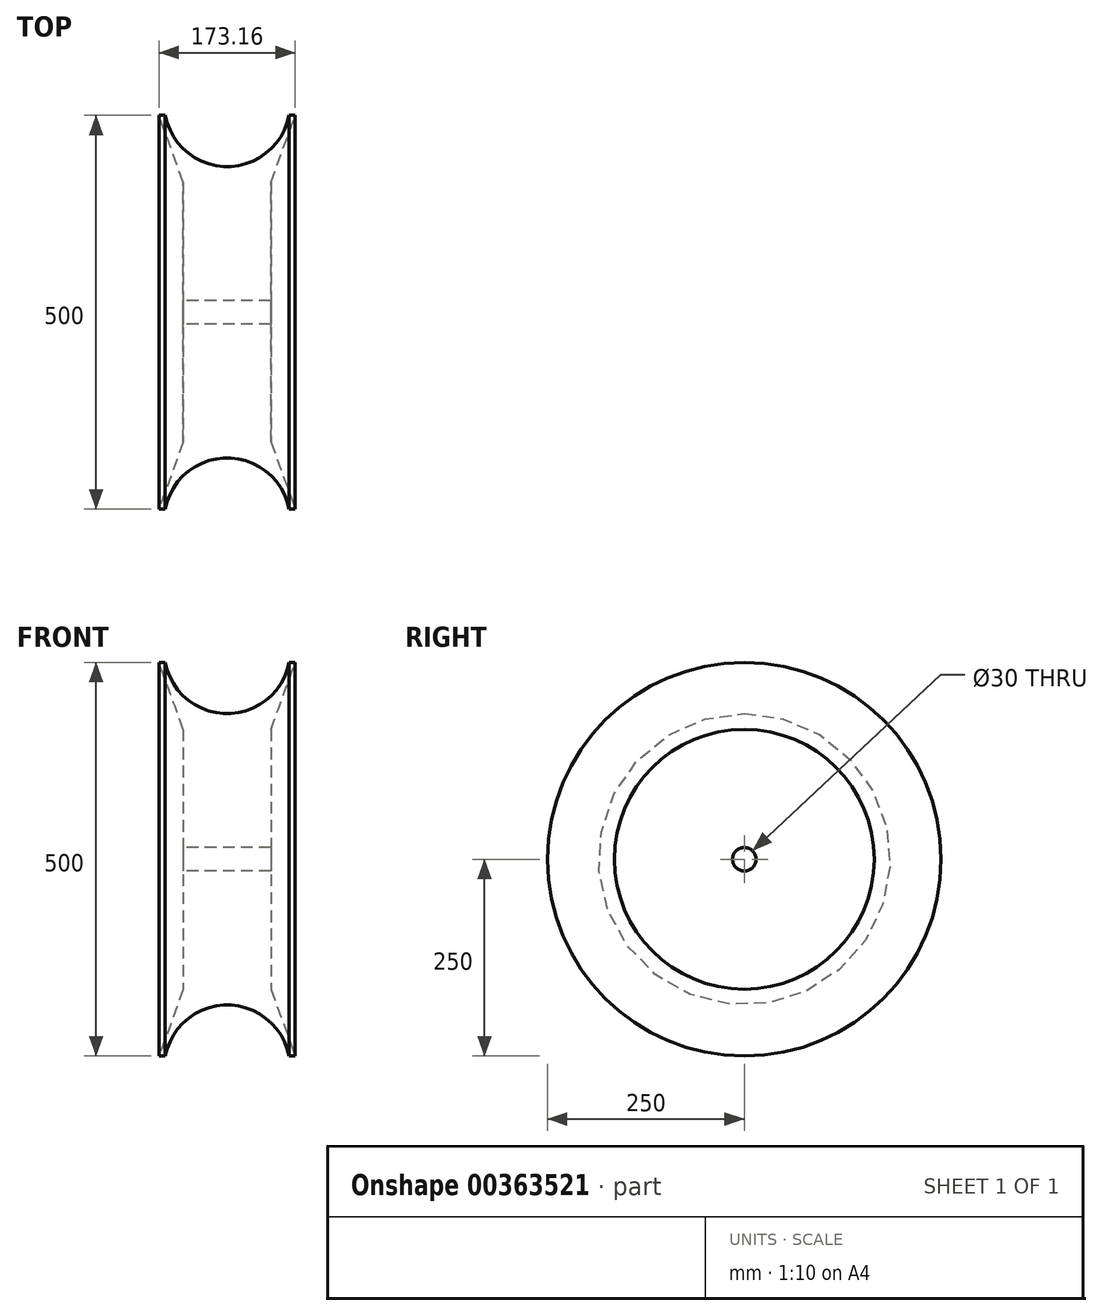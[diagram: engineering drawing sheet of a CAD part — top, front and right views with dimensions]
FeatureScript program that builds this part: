
annotation { "Feature Type Name" : "Feature", "Feature Type Description" : "" }
export const myFeature = defineFeature(function(context is Context, id is Id, definition is map)
    precondition{}
    {
        {
            var Q0;
            Q0=qCreatedBy(makeId("Front.planeOp"),FACE);
            var sketch = newSketch(context, id + "F0", { "sketchPlane" : qUnion([Q0])});
            skLineSegment(sketch, "E0", {"start": v(55.64, 15) * mm, "end": v(55.64, 165) * mm});
            skLineSegment(sketch, "E1", {"start": v(55.64, 165) * mm, "end": v(86.58, 250) * mm});
            skLineSegment(sketch, "E2", {"start": v(0, -26.36) * mm, "end": v(0, 300.42) * mm, "construction": true});
            skLineSegment(sketch, "E3", {"start": v(86.58, 250) * mm, "end": v(78.58, 250) * mm});
            skArc(sketch, "E4", {"start": v(0, 185) * mm, "mid": v(51, 203.36) * mm, "end": v(78.58, 250) * mm});
            skLineSegment(sketch, "E5", {"start": v(0, 185) * mm, "end": v(0, 0) * mm});
            skLineSegment(sketch, "E6", {"start": v(0, 15) * mm, "end": v(55.64, 15) * mm});
            skLineSegment(sketch, "E7", {"start": v(-86.07, 0) * mm, "end": v(75.22, 0) * mm, "construction": true});
            skSolve(sketch);
        }
        {
            var Q0;
            Q0=makeQuery(id+"F0.imprint","IMPRINT",FACE,{"disambiguationData":[TD([[makeQuery(id+"F0.imprint","IMPRINT",EDGE,{"derivedFrom":sQuery(id+"F0.wireOp",EDGE,"E0")}),1.0]])]});
            var Q1;
            Q1=sQuery(id+"F0.wireOp",EDGE,"E7");
            revolve(context, id + "F1", {"entities" : qUnion([Q0]), "axis" : qUnion([Q1]), "revolveType" : RevolveType.FULL});
        }
        {
            var Q0;
            Q0=makeQuery(id+"F1.opRevolve","SWEPT_BODY",BODY,{"disambiguationData":[OSD([sQuery(id+"F0.wireOp",EDGE,"NzdFl3dr-dBQ1-Urvl-hef5-xC6ee6wVBlBB"),sQuery(id+"F0.wireOp",EDGE,"E0"),sQuery(id+"F0.wireOp",EDGE,"E1"),sQuery(id+"F0.wireOp",EDGE,"E3"),sQuery(id+"F0.wireOp",EDGE,"E4"),sQuery(id+"F0.wireOp",EDGE,"E5")])]});
            var Q1;
            Q1=qCreatedBy(makeId("Right.planeOp"),FACE);
            mirror(context, id + "F2", {"operationType" : NewBodyOperationType.ADD, "entities" : qUnion([Q0]), "mirrorPlane" : qUnion([Q1])});
        }
    });
